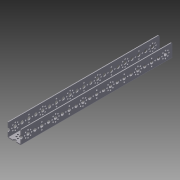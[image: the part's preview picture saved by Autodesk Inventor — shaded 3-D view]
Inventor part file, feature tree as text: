
AUTODESK INVENTOR PART (.ipt)
format: ipt  version: 2014 SP2 (Build 180246200, 246)  size: 755,200 bytes
history: native  units: in
note: dims shown in document units (in); Inventor stores cm internally (conversion verified against a paired STEP export)
features: other x1, extrude x1, imported_body x1, sketch x1
ambient origin geometry x8: Origin, YZ Plane, XZ Plane, XY Plane, X Axis, Y Axis, Z Axis, Center Point
bodies: Solid1 (feature_tree)
feature tree (4):
  other  "416mm Channel.sat1"
  extrude  "Extrusion1"  Depth=3.937in TaperAngle=0.0deg
  imported_body  "Base1"
  sketch  "Sketch1"  dims[d0=3.0in d1=3.937in d2=0.0in d4=0.0in]
